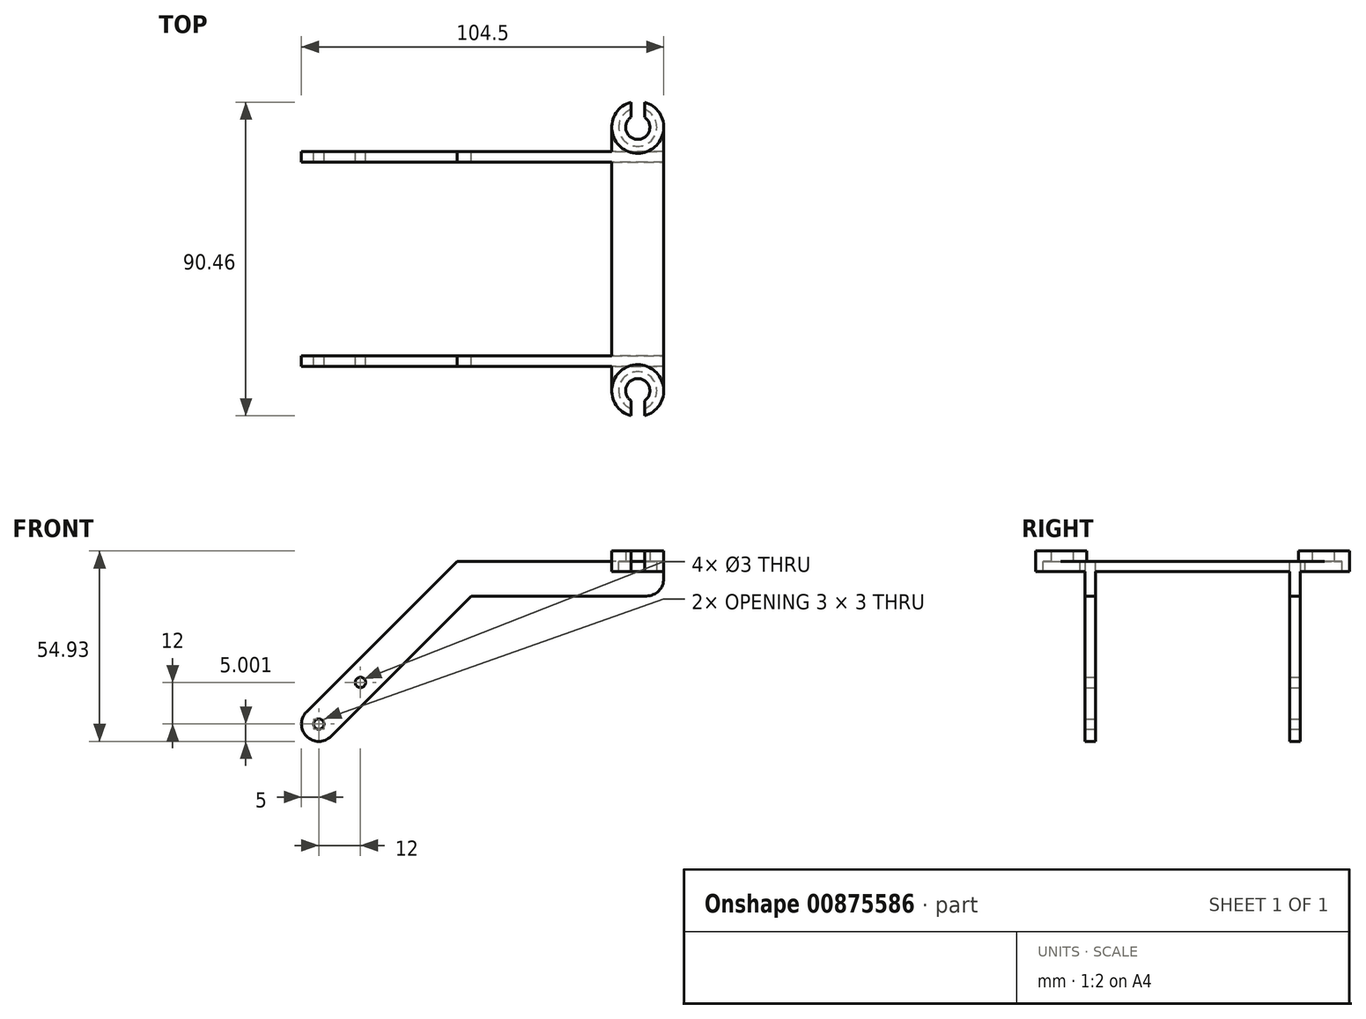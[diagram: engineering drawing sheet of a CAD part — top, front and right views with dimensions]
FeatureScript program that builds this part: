
annotation { "Feature Type Name" : "Feature", "Feature Type Description" : "" }
export const myFeature = defineFeature(function(context is Context, id is Id, definition is map)
    precondition{}
    {
        {
            var Q0;
            Q0=qCreatedBy(makeId("Front.planeOp"),FACE);
            var sketch = newSketch(context, id + "F0", { "sketchPlane" : qUnion([Q0])});
            skLineSegment(sketch, "E0", {"start": v(3.54, 3.54) * mm, "end": v(44, 44) * mm});
            skLineSegment(sketch, "E1", {"start": v(44, 44) * mm, "end": v(94.5, 44) * mm});
            skLineSegment(sketch, "E2", {"start": v(99.5, 49) * mm, "end": v(99.5, 54) * mm});
            skLineSegment(sketch, "E3", {"start": v(99.5, 54) * mm, "end": v(39.86, 54) * mm});
            skLineSegment(sketch, "E4", {"start": v(-3.54, 3.54) * mm, "end": v(-3.54, 3.54) * mm});
            skLineSegment(sketch, "E5", {"start": v(-3.54, 10.6) * mm, "end": v(39.86, 54) * mm});
            skPoint(sketch, "E6.visualSharp", {"position": v(99.5, 44) * mm});
            skArc(sketch, "E6.filletArc", {"start": v(94.5, 44) * mm, "mid": v(98.04, 45.46) * mm, "end": v(99.5, 49) * mm});
            skPoint(sketch, "E7.visualSharp", {"position": v(-7.07, 7.07) * mm});
            skArc(sketch, "E7.filletArc", {"start": v(-3.54, 10.6) * mm, "mid": v(-5, 7.07) * mm, "end": v(-3.54, 3.54) * mm});
            skPoint(sketch, "E8.visualSharp", {"position": v(0, 0) * mm});
            skArc(sketch, "E8.filletArc", {"start": v(-3.54, 3.54) * mm, "mid": v(0, 2.07) * mm, "end": v(3.54, 3.54) * mm});
            skCircle(sketch, "E9", {"center": v(0, 7.07) * mm, "radius": 1.5 * mm});
            skCircle(sketch, "E10", {"center": v(12, 19.07) * mm, "radius": 1.5 * mm});
            skSolve(sketch);
        }
        {
            var Q0;
            Q0=makeQuery(id+"F0.imprint","IMPRINT",FACE,{"disambiguationData":[TD([[makeQuery(id+"F0.imprint","IMPRINT",EDGE,{"derivedFrom":sQuery(id+"F0.wireOp",EDGE,"E0")}),1.0]])]});
            extrude(context, id + "F1", {"entities" : qUnion([Q0]), "depth" : 62 * mm, "offsetDistance" : 25 * mm});
        }
        {
            var Q0;
            Q0=makeQuery(id+"F1.opExtrude","SWEPT_FACE",FACE,{"disambiguationData":[OSD([sQuery(id+"F0.wireOp",EDGE,"E3")])]});
            var sketch = newSketch(context, id + "F2", { "sketchPlane" : qUnion([Q0])});
            skLineSegment(sketch, "E11.bottom", {"start": v(99.5, -3) * mm, "end": v(-20.5, -3) * mm});
            skLineSegment(sketch, "E11.top", {"start": v(99.5, -59) * mm, "end": v(-20.5, -59) * mm});
            skLineSegment(sketch, "E11.left", {"start": v(99.5, -3) * mm, "end": v(99.5, -59) * mm});
            skLineSegment(sketch, "E11.right", {"start": v(-20.5, -3) * mm, "end": v(-20.5, -59) * mm});
            skSolve(sketch);
        }
        {
            var Q0;
            {var subQ0=sQuery(id+"F2.wireOp",EDGE,"E11.right");Q0=makeQuery(id+"F2.imprint","IMPRINT",FACE,{"disambiguationData":[TD([[makeQuery(id+"F2.imprint","IMPRINT",EDGE,{"derivedFrom":subQ0}),1.0]])]});}
            var Q1;
            {var subQ0=sQuery(id+"F2.wireOp",EDGE,"E11.left");Q1=makeQuery(id+"F2.imprint","IMPRINT",FACE,{"disambiguationData":[TD([[makeQuery(id+"F2.imprint","IMPRINT",EDGE,{"derivedFrom":subQ0}),1.0]])]});}
            extrude(context, id + "F3", {"entities" : qUnion([Q0, Q1]), "operationType" : NewBodyOperationType.REMOVE, "oppositeDirection" : true, "depth" : 100 * mm, "offsetDistance" : 25 * mm});
        }
        {
            var Q0;
            {var subQ1=sQuery(id+"F0.wireOp",EDGE,"E3");Q0=makeQuery(id+"F3.boolean.opBoolean","SPLIT",FACE,{"disambiguationData":[TD([makeQuery(id+"F3.opExtrude","SWEPT_FACE",FACE,{"disambiguationData":[OSD([sQuery(id+"F2.wireOp",EDGE,"E11.bottom")])]})])],"derivedFrom":makeQuery(id+"F1.opExtrude","SWEPT_FACE",FACE,{"disambiguationData":[OSD([subQ1])]})});}
            var sketch = newSketch(context, id + "F4", { "sketchPlane" : qUnion([Q0])});
            skLineSegment(sketch, "E12.bottom", {"start": v(92, 14.5) * mm, "end": v(92, 14.5) * mm});
            skLineSegment(sketch, "E12.top", {"start": v(92, -76.5) * mm, "end": v(92, -76.5) * mm});
            skLineSegment(sketch, "E12.left", {"start": v(84.5, 7) * mm, "end": v(84.5, -69) * mm});
            skLineSegment(sketch, "E12.right", {"start": v(99.5, 7) * mm, "end": v(99.5, -69) * mm});
            skPoint(sketch, "E13.visualSharp", {"position": v(84.5, 14.5) * mm});
            skArc(sketch, "E13.filletArc", {"start": v(92, 14.5) * mm, "mid": v(86.7, 12.3) * mm, "end": v(84.5, 7) * mm});
            skPoint(sketch, "E14.visualSharp", {"position": v(99.5, 14.5) * mm});
            skArc(sketch, "E14.filletArc", {"start": v(99.5, 7) * mm, "mid": v(97.3, 12.3) * mm, "end": v(92, 14.5) * mm});
            skPoint(sketch, "E15.visualSharp", {"position": v(84.5, -76.5) * mm});
            skArc(sketch, "E15.filletArc", {"start": v(84.5, -69) * mm, "mid": v(86.7, -74.3) * mm, "end": v(92, -76.5) * mm});
            skPoint(sketch, "E16.visualSharp", {"position": v(99.5, -76.5) * mm});
            skArc(sketch, "E16.filletArc", {"start": v(92, -76.5) * mm, "mid": v(97.3, -74.3) * mm, "end": v(99.5, -69) * mm});
            skCircle(sketch, "E17", {"center": v(92, 7) * mm, "radius": 5.5 * mm});
            skCircle(sketch, "E18", {"center": v(92, 7) * mm, "radius": 7.5 * mm});
            skCircle(sketch, "E19", {"center": v(92, -69) * mm, "radius": 5.5 * mm});
            skCircle(sketch, "E20", {"center": v(92, -69) * mm, "radius": 7.5 * mm});
            skLineSegment(sketch, "E21", {"start": v(94, 12.12) * mm, "end": v(94, 14.23) * mm});
            skLineSegment(sketch, "E22", {"start": v(90, 12.12) * mm, "end": v(90, 14.23) * mm});
            skLineSegment(sketch, "E23", {"start": v(94, -74.12) * mm, "end": v(94, -76.23) * mm});
            skLineSegment(sketch, "E24", {"start": v(90, -74.12) * mm, "end": v(90, -76.23) * mm});
            skSolve(sketch);
        }
        {
            var Q0;
            {var subQ0=sQuery(id+"F4.wireOp",EDGE,"E23");Q0=makeQuery(id+"F4.imprint","IMPRINT",FACE,{"disambiguationData":[TD([[makeQuery(id+"F4.imprint","IMPRINT",EDGE,{"derivedFrom":subQ0}),1.0]])]});}
            var Q1;
            {var subQ0=sQuery(id+"F4.wireOp",EDGE,"E18");var subQ1=sQuery(id+"F4.wireOp",EDGE,"E12.left");var subQ2=makeQuery(id+"F4.imprint","INTERSECT",VERTEX,{"derivedFrom":[subQ1,subQ0]});Q1=makeQuery(id+"F4.imprint","IMPRINT",FACE,{"disambiguationData":[TD([[makeQuery(id+"F4.imprint","IMPRINT",EDGE,{"disambiguationData":[TD([[subQ2,-1.0]])],"derivedFrom":subQ1}),1.0]])]});}
            var Q2;
            {var subQ0=sQuery(id+"F4.wireOp",EDGE,"E20");var subQ1=sQuery(id+"F4.wireOp",EDGE,"E12.left");var subQ2=makeQuery(id+"F4.imprint","INTERSECT",VERTEX,{"derivedFrom":[subQ1,subQ0]});Q2=makeQuery(id+"F4.imprint","IMPRINT",FACE,{"disambiguationData":[TD([[makeQuery(id+"F4.imprint","IMPRINT",EDGE,{"disambiguationData":[TD([[subQ2,1.0]])],"derivedFrom":subQ1}),1.0]])]});}
            var Q3;
            {var subQ0=sQuery(id+"F4.wireOp",EDGE,"E12.right");var subQ1=makeQuery(id+"F1.opExtrude","CAP_EDGE",EDGE,{"disambiguationData":[OSD([sQuery(id+"F0.wireOp",EDGE,"E3")])],"isStart":true});var subQ2=makeQuery(id+"F4.imprint","INTERSECT",VERTEX,{"derivedFrom":[subQ1,subQ0]});var subQ3=sQuery(id+"F4.wireOp",EDGE,"E18");var subQ4=makeQuery(id+"F4.imprint","INTERSECT",VERTEX,{"derivedFrom":[subQ0,subQ3]});Q3=makeQuery(id+"F4.imprint","IMPRINT",FACE,{"disambiguationData":[TD([[makeQuery(id+"F4.imprint","IMPRINT",EDGE,{"disambiguationData":[TD([[subQ2,1.0],[subQ4,-1.0]])],"derivedFrom":subQ0}),-1.0]])]});}
            var Q4;
            {var subQ0=sQuery(id+"F4.wireOp",EDGE,"E18");var subQ1=makeQuery(id+"F1.opExtrude","CAP_EDGE",EDGE,{"disambiguationData":[OSD([sQuery(id+"F0.wireOp",EDGE,"E3")])],"isStart":true});var subQ2=makeQuery(id+"F4.imprint","INTERSECT",VERTEX,{"disambiguationData":[OD(0.0)],"derivedFrom":[subQ1,subQ0]});Q4=makeQuery(id+"F4.imprint","IMPRINT",FACE,{"disambiguationData":[TD([[makeQuery(id+"F4.imprint","IMPRINT",EDGE,{"disambiguationData":[TD([[subQ2,-1.0]])],"derivedFrom":subQ0}),1.0]])]});}
            var Q5;
            {var subQ6=sQuery(id+"F4.wireOp",EDGE,"E21");Q5=makeQuery(id+"F4.imprint","IMPRINT",FACE,{"disambiguationData":[TD([[makeQuery(id+"F4.imprint","IMPRINT",EDGE,{"derivedFrom":subQ6}),-1.0]])]});}
            var Q6;
            {var subQ1=makeQuery(id+"F1.opExtrude","CAP_EDGE",EDGE,{"disambiguationData":[OSD([sQuery(id+"F0.wireOp",EDGE,"E3")])],"isStart":true});var subQ4=sQuery(id+"F4.wireOp",EDGE,"E12.left");var subQ5=makeQuery(id+"F4.imprint","INTERSECT",VERTEX,{"derivedFrom":[subQ1,subQ4]});Q6=makeQuery(id+"F4.imprint","IMPRINT",FACE,{"disambiguationData":[TD([[makeQuery(id+"F4.imprint","IMPRINT",EDGE,{"disambiguationData":[TD([[subQ5,-1.0]])],"derivedFrom":subQ4}),1.0]])]});}
            extrude(context, id + "F5", {"entities" : qUnion([Q0, Q1, Q2, Q3, Q4, Q5, Q6]), "oppositeDirection" : true, "depth" : 3 * mm, "offsetDistance" : 25 * mm});
        }
        {
            var Q0;
            Q0=makeQuery(id+"F3.boolean.opBoolean","SPLIT",BODY,{"disambiguationData":[OD(0.0)],"derivedFrom":makeQuery(id+"F1.opExtrude","SWEPT_BODY",BODY,{"disambiguationData":[OSD([sQuery(id+"F0.wireOp",EDGE,"E0"),sQuery(id+"F0.wireOp",EDGE,"E1"),sQuery(id+"F0.wireOp",EDGE,"E2"),sQuery(id+"F0.wireOp",EDGE,"E3"),sQuery(id+"F0.wireOp",EDGE,"E5"),sQuery(id+"F0.wireOp",EDGE,"E6.filletArc"),sQuery(id+"F0.wireOp",EDGE,"E7.filletArc"),sQuery(id+"F0.wireOp",EDGE,"E8.filletArc"),sQuery(id+"F0.wireOp",EDGE,"E9"),sQuery(id+"F0.wireOp",EDGE,"E10")])]})});
            var Q1;
            Q1=makeQuery(id+"F3.boolean.opBoolean","SPLIT",BODY,{"disambiguationData":[OD(1.0)],"derivedFrom":makeQuery(id+"F1.opExtrude","SWEPT_BODY",BODY,{"disambiguationData":[OSD([sQuery(id+"F0.wireOp",EDGE,"E0"),sQuery(id+"F0.wireOp",EDGE,"E1"),sQuery(id+"F0.wireOp",EDGE,"E2"),sQuery(id+"F0.wireOp",EDGE,"E3"),sQuery(id+"F0.wireOp",EDGE,"E5"),sQuery(id+"F0.wireOp",EDGE,"E6.filletArc"),sQuery(id+"F0.wireOp",EDGE,"E7.filletArc"),sQuery(id+"F0.wireOp",EDGE,"E8.filletArc"),sQuery(id+"F0.wireOp",EDGE,"E9"),sQuery(id+"F0.wireOp",EDGE,"E10")])]})});
            var Q2;
            Q2=makeQuery(id+"F5.opExtrude","SWEPT_BODY",BODY,{"disambiguationData":[OSD([sQuery(id+"F4.wireOp",EDGE,"E12.left"),sQuery(id+"F4.wireOp",EDGE,"E12.right"),sQuery(id+"F4.wireOp",EDGE,"E17"),sQuery(id+"F4.wireOp",EDGE,"E18"),sQuery(id+"F4.wireOp",EDGE,"E19"),sQuery(id+"F4.wireOp",EDGE,"E20"),sQuery(id+"F4.wireOp",EDGE,"E21"),sQuery(id+"F4.wireOp",EDGE,"E22"),sQuery(id+"F4.wireOp",EDGE,"E23"),sQuery(id+"F4.wireOp",EDGE,"E24")])]});
            booleanBodies(context, id + "F6", {"operationType" : BooleanOperationType.UNION, "tools" : qUnion([Q0, Q1, Q2])});
        }
        {
            var Q0;
            {var subQ6=sQuery(id+"F0.wireOp",EDGE,"E3");var subQ12=makeQuery(id+"F1.opExtrude","SWEPT_FACE",FACE,{"disambiguationData":[OSD([subQ6])]});Q0=makeQuery(id+"F6.opBoolean","MERGE",FACE,{"derivedFrom":[makeQuery(id+"F3.boolean.opBoolean","SPLIT",FACE,{"disambiguationData":[TD([makeQuery(id+"F3.opExtrude","SWEPT_FACE",FACE,{"disambiguationData":[OSD([sQuery(id+"F2.wireOp",EDGE,"E11.bottom")])]})])],"derivedFrom":subQ12}),makeQuery(id+"F3.boolean.opBoolean","SPLIT",FACE,{"disambiguationData":[TD([makeQuery(id+"F3.opExtrude","SWEPT_FACE",FACE,{"disambiguationData":[OSD([sQuery(id+"F2.wireOp",EDGE,"E11.top")])]})])],"derivedFrom":subQ12}),makeQuery(id+"F5.opExtrude","CAP_FACE",FACE,{"disambiguationData":[OSD([sQuery(id+"F4.wireOp",EDGE,"E12.left"),sQuery(id+"F4.wireOp",EDGE,"E12.right"),sQuery(id+"F4.wireOp",EDGE,"E17"),sQuery(id+"F4.wireOp",EDGE,"E18"),sQuery(id+"F4.wireOp",EDGE,"E19"),sQuery(id+"F4.wireOp",EDGE,"E20"),sQuery(id+"F4.wireOp",EDGE,"E21"),sQuery(id+"F4.wireOp",EDGE,"E22"),sQuery(id+"F4.wireOp",EDGE,"E23"),sQuery(id+"F4.wireOp",EDGE,"E24")])],"isStart":true})]});}
            var sketch = newSketch(context, id + "F7", { "sketchPlane" : qUnion([Q0])});
            skCircle(sketch, "E25", {"center": v(92, 7) * mm, "radius": 7.5 * mm});
            skCircle(sketch, "E26", {"center": v(92, 7) * mm, "radius": 3.5 * mm});
            skLineSegment(sketch, "E27", {"start": v(90, 14.23) * mm, "end": v(90, 9.87) * mm});
            skLineSegment(sketch, "E28", {"start": v(94, 14.23) * mm, "end": v(94, 9.87) * mm});
            skCircle(sketch, "E29", {"center": v(92, -69) * mm, "radius": 7.5 * mm});
            skCircle(sketch, "E30", {"center": v(92, -69) * mm, "radius": 3.5 * mm});
            skLineSegment(sketch, "E31", {"start": v(90, -76.23) * mm, "end": v(90, -71.87) * mm});
            skLineSegment(sketch, "E32", {"start": v(94, -76.23) * mm, "end": v(94, -71.87) * mm});
            skSolve(sketch);
        }
        {
            var Q0;
            {var subQ1=sQuery(id+"F4.wireOp",EDGE,"E17");var subQ2=makeQuery(id+"F5.opExtrude","CAP_EDGE",EDGE,{"disambiguationData":[OSD([subQ1])],"isStart":true});Q0=makeQuery(id+"F7.imprint","IMPRINT",FACE,{"disambiguationData":[TD([[makeQuery(id+"F7.imprint","IMPRINT",EDGE,{"derivedFrom":subQ2}),-1.0]])]});}
            var Q1;
            {var subQ5=makeQuery(id+"F5.opExtrude","CAP_EDGE",EDGE,{"disambiguationData":[OSD([sQuery(id+"F4.wireOp",EDGE,"E17")])],"isStart":true});Q1=makeQuery(id+"F7.imprint","IMPRINT",FACE,{"disambiguationData":[TD([[makeQuery(id+"F7.imprint","IMPRINT",EDGE,{"derivedFrom":subQ5}),1.0]])]});}
            var Q2;
            {var subQ20=sQuery(id+"F4.wireOp",EDGE,"E19");var subQ21=makeQuery(id+"F5.opExtrude","CAP_EDGE",EDGE,{"disambiguationData":[OSD([subQ20])],"isStart":true});Q2=makeQuery(id+"F7.imprint","IMPRINT",FACE,{"disambiguationData":[TD([[makeQuery(id+"F7.imprint","IMPRINT",EDGE,{"derivedFrom":subQ21}),-1.0]])]});}
            var Q3;
            {var subQ5=makeQuery(id+"F5.opExtrude","CAP_EDGE",EDGE,{"disambiguationData":[OSD([sQuery(id+"F4.wireOp",EDGE,"E19")])],"isStart":true});Q3=makeQuery(id+"F7.imprint","IMPRINT",FACE,{"disambiguationData":[TD([[makeQuery(id+"F7.imprint","IMPRINT",EDGE,{"derivedFrom":subQ5}),1.0]])]});}
            extrude(context, id + "F8", {"entities" : qUnion([Q0, Q1, Q2, Q3]), "operationType" : NewBodyOperationType.ADD, "depth" : 3 * mm, "offsetDistance" : 25 * mm});
        }
    });
